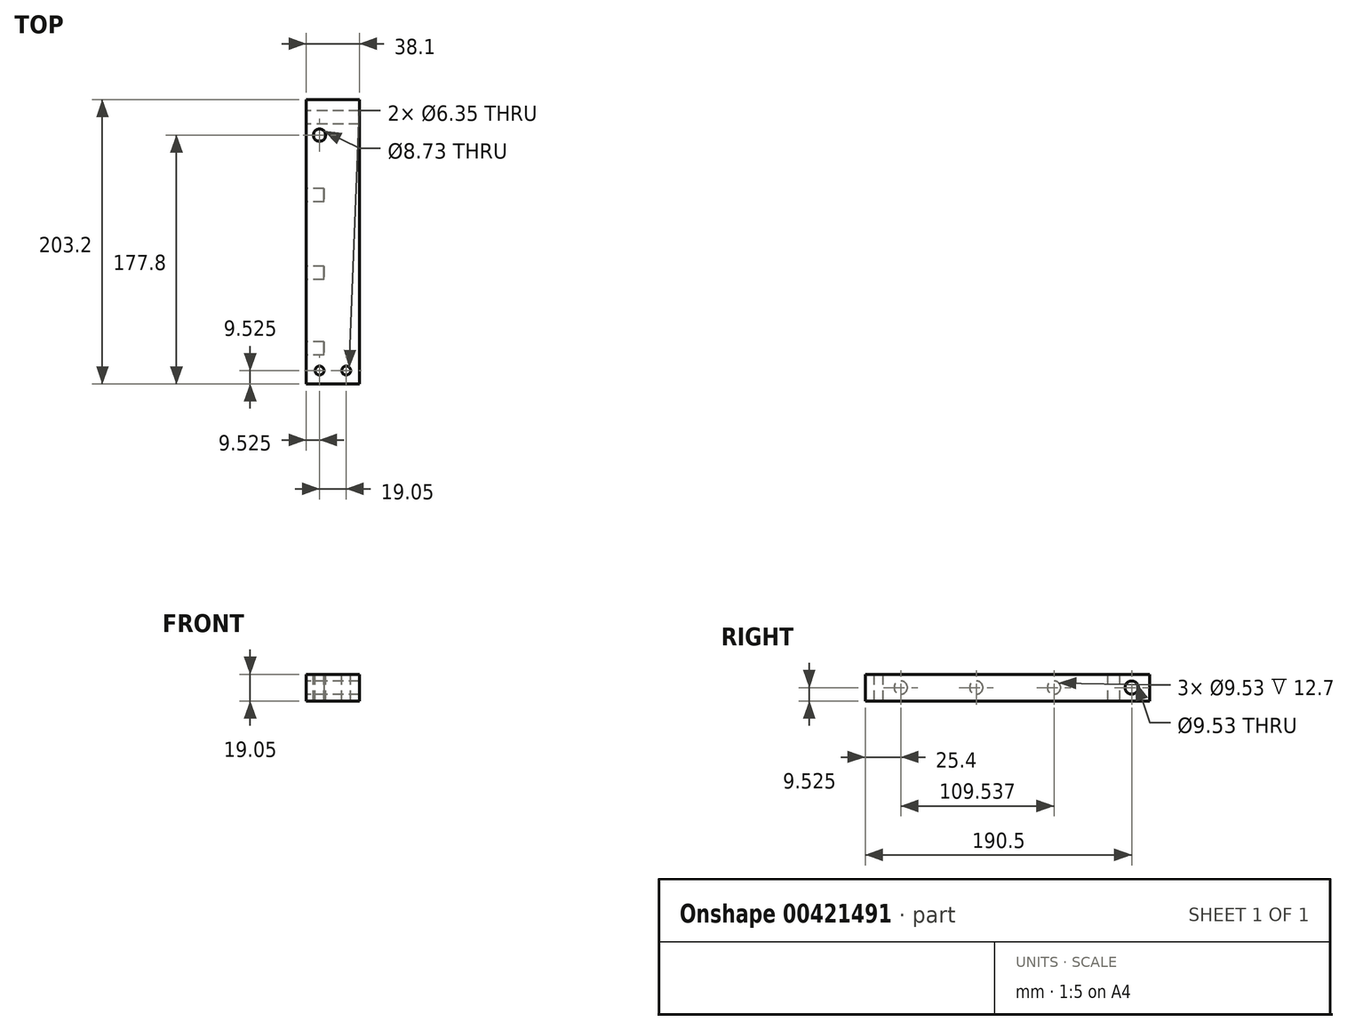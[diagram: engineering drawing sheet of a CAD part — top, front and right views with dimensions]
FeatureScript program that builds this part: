
annotation { "Feature Type Name" : "Feature", "Feature Type Description" : "" }
export const myFeature = defineFeature(function(context is Context, id is Id, definition is map)
    precondition{}
    {
        {
            var Q0;
            Q0=qCreatedBy(makeId("Top.planeOp"),FACE);
            var sketch = newSketch(context, id + "F0", { "sketchPlane" : qUnion([Q0])});
            skLineSegment(sketch, "E0.bottom", {"start": v(19.05, 101.6) * mm, "end": v(-19.05, 101.6) * mm});
            skLineSegment(sketch, "E0.top", {"start": v(19.05, -101.6) * mm, "end": v(-19.05, -101.6) * mm});
            skLineSegment(sketch, "E0.left", {"start": v(19.05, 101.6) * mm, "end": v(19.05, -101.6) * mm});
            skLineSegment(sketch, "E0.right", {"start": v(-19.05, 101.6) * mm, "end": v(-19.05, -101.6) * mm});
            skPoint(sketch, "E0.middle", {"position": v(0, 0) * mm});
            skSolve(sketch);
        }
        {
            var Q0;
            Q0=makeQuery(id+"F0.imprint","IMPRINT",FACE,{"disambiguationData":[TD([[makeQuery(id+"F0.imprint","IMPRINT",EDGE,{"derivedFrom":sQuery(id+"F0.wireOp",EDGE,"E0.bottom")}),1.0]])]});
            extrude(context, id + "F1", {"entities" : qUnion([Q0]), "depth" : 19.05 * mm});
        }
        {
            var Q0;
            Q0=makeQuery(id+"F1.opExtrude","CAP_FACE",FACE,{"disambiguationData":[OSD([sQuery(id+"F0.wireOp",EDGE,"E0.bottom"),sQuery(id+"F0.wireOp",EDGE,"E0.top"),sQuery(id+"F0.wireOp",EDGE,"E0.left"),sQuery(id+"F0.wireOp",EDGE,"E0.right")])],"isStart":false});
            var sketch = newSketch(context, id + "F2", { "sketchPlane" : qUnion([Q0])});
            skLineSegment(sketch, "E1", {"start": v(-19.05, -92.08) * mm, "end": v(19.05, -92.07) * mm, "construction": true});
            skCircle(sketch, "E2", {"center": v(-9.52, -92.08) * mm, "radius": 3.18 * mm});
            skCircle(sketch, "E3", {"center": v(9.53, -92.08) * mm, "radius": 3.18 * mm});
            skSolve(sketch);
        }
        {
            var Q0;
            Q0=qSketchRegion(id+"F2",true);
            extrude(context, id + "F3", {"entities" : qUnion([Q0]), "operationType" : NewBodyOperationType.REMOVE, "endBound" : BoundingType.THROUGH_ALL, "oppositeDirection" : true, "depth" : 25.4 * mm});
        }
        {
            var Q0;
            Q0=makeQuery(id+"F1.opExtrude","CAP_FACE",FACE,{"disambiguationData":[OSD([sQuery(id+"F0.wireOp",EDGE,"E0.bottom"),sQuery(id+"F0.wireOp",EDGE,"E0.top"),sQuery(id+"F0.wireOp",EDGE,"E0.left"),sQuery(id+"F0.wireOp",EDGE,"E0.right")])],"isStart":false});
            var sketch = newSketch(context, id + "F4", { "sketchPlane" : qUnion([Q0])});
            skCircle(sketch, "E4", {"center": v(-9.53, 76.2) * mm, "radius": 4.37 * mm});
            skSolve(sketch);
        }
        {
            var Q0;
            Q0=qSketchRegion(id+"F4",true);
            extrude(context, id + "F5", {"entities" : qUnion([Q0]), "operationType" : NewBodyOperationType.REMOVE, "endBound" : BoundingType.THROUGH_ALL, "oppositeDirection" : true, "depth" : 25.4 * mm});
        }
        {
            var Q0;
            Q0=makeQuery(id+"F1.opExtrude","SWEPT_FACE",FACE,{"disambiguationData":[OSD([sQuery(id+"F0.wireOp",EDGE,"E0.right")])]});
            var sketch = newSketch(context, id + "F6", { "sketchPlane" : qUnion([Q0])});
            skLineSegment(sketch, "E5", {"start": v(-101.6, 9.53) * mm, "end": v(101.6, 9.53) * mm, "construction": true});
            skCircle(sketch, "E6", {"center": v(-33.34, 9.52) * mm, "radius": 4.76 * mm});
            skCircle(sketch, "E7", {"center": v(22.22, 9.53) * mm, "radius": 4.76 * mm});
            skCircle(sketch, "E8", {"center": v(76.2, 9.53) * mm, "radius": 4.76 * mm});
            skCircle(sketch, "E9", {"center": v(-88.9, 9.52) * mm, "radius": 4.76 * mm});
            skSolve(sketch);
        }
        {
            var Q0;
            Q0=makeQuery(id+"F6.imprint","IMPRINT",FACE,{"disambiguationData":[TD([[makeQuery(id+"F6.imprint","IMPRINT",EDGE,{"derivedFrom":sQuery(id+"F6.wireOp",EDGE,"E9")}),1.0]])]});
            var Q1;
            Q1=sQuery(id+"F6.wireOp",EDGE,"E5");
            var Q2;
            Q2=sQuery(id+"F6.wireOp",EDGE,"E9");
            extrude(context, id + "F7", {"entities" : qUnion([Q0]), "operationType" : NewBodyOperationType.REMOVE, "surfaceEntities" : qUnion([Q1, Q2]), "endBound" : BoundingType.THROUGH_ALL, "oppositeDirection" : true, "depth" : 25.4 * mm});
        }
        {
            var Q0;
            Q0=makeQuery(id+"F6.imprint","IMPRINT",FACE,{"disambiguationData":[TD([[makeQuery(id+"F6.imprint","IMPRINT",EDGE,{"derivedFrom":sQuery(id+"F6.wireOp",EDGE,"E6")}),1.0]])]});
            var Q1;
            Q1=makeQuery(id+"F6.imprint","IMPRINT",FACE,{"disambiguationData":[TD([[makeQuery(id+"F6.imprint","IMPRINT",EDGE,{"derivedFrom":sQuery(id+"F6.wireOp",EDGE,"E7")}),1.0]])]});
            var Q2;
            Q2=makeQuery(id+"F6.imprint","IMPRINT",FACE,{"disambiguationData":[TD([[makeQuery(id+"F6.imprint","IMPRINT",EDGE,{"derivedFrom":sQuery(id+"F6.wireOp",EDGE,"E8")}),1.0]])]});
            extrude(context, id + "F8", {"entities" : qUnion([Q0, Q1, Q2]), "operationType" : NewBodyOperationType.REMOVE, "oppositeDirection" : true, "depth" : 12.7 * mm});
        }
    });
